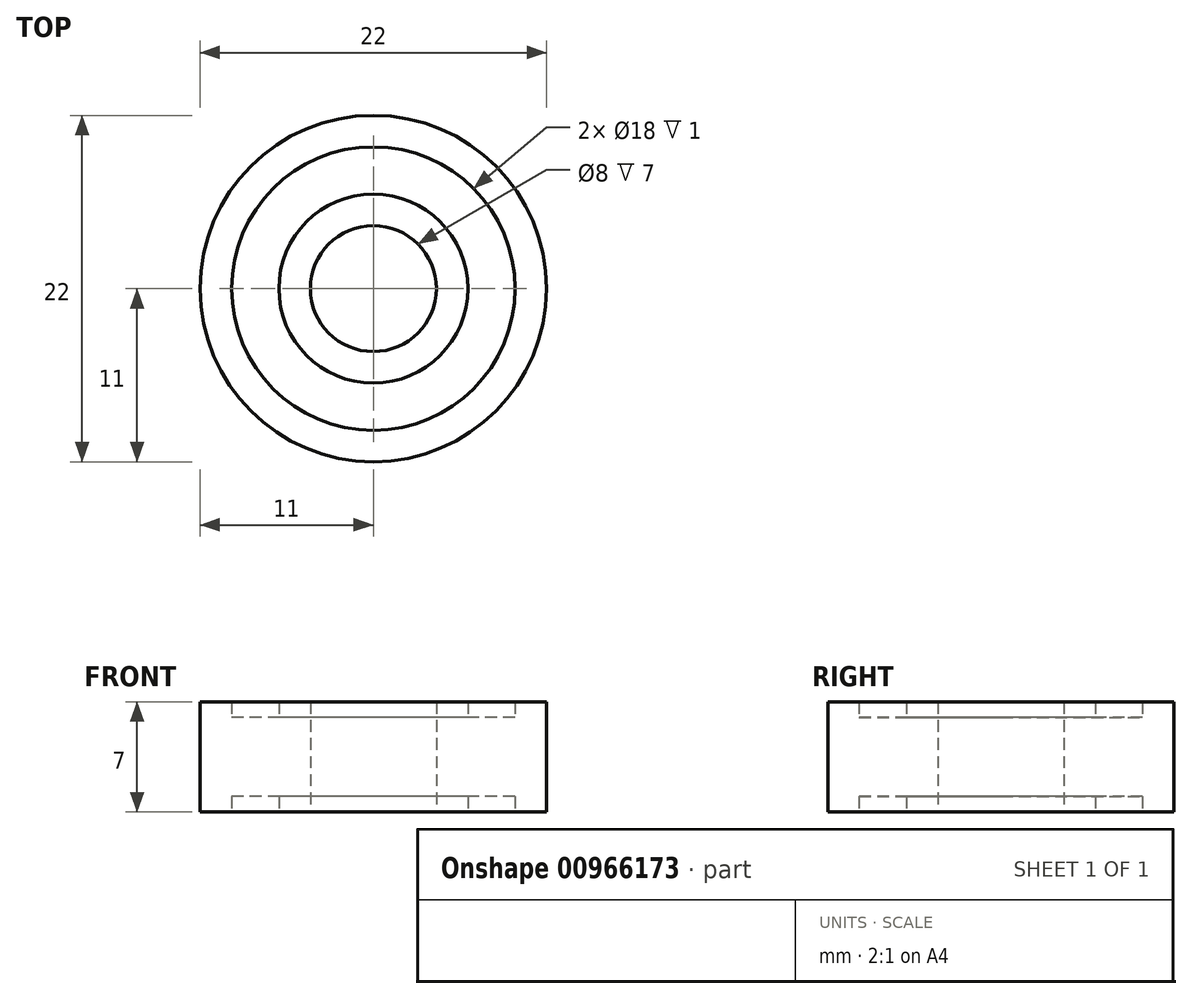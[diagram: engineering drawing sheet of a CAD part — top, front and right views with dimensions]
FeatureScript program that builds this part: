
annotation { "Feature Type Name" : "Feature", "Feature Type Description" : "" }
export const myFeature = defineFeature(function(context is Context, id is Id, definition is map)
    precondition{}
    {
        {
            var Q0;
            Q0=qCreatedBy(makeId("Top.planeOp"),FACE);
            var sketch = newSketch(context, id + "F0", { "sketchPlane" : qUnion([Q0])});
            skCircle(sketch, "E0", {"center": v(0, 0) * mm, "radius": 11 * mm});
            skCircle(sketch, "E1", {"center": v(0, 0) * mm, "radius": 4 * mm});
            skCircle(sketch, "E2", {"center": v(0, 0) * mm, "radius": 9 * mm});
            skCircle(sketch, "E3", {"center": v(0, 0) * mm, "radius": 6 * mm});
            skSolve(sketch);
        }
        {
            var Q0;
            Q0=makeQuery(id+"F0.imprint","IMPRINT",FACE,{"disambiguationData":[TD([[makeQuery(id+"F0.imprint","IMPRINT",EDGE,{"derivedFrom":sQuery(id+"F0.wireOp",EDGE,"E0")}),1.0]])]});
            var Q1;
            Q1=makeQuery(id+"F0.imprint","IMPRINT",FACE,{"disambiguationData":[TD([[makeQuery(id+"F0.imprint","IMPRINT",EDGE,{"derivedFrom":sQuery(id+"F0.wireOp",EDGE,"E1")}),-1.0]])]});
            extrude(context, id + "F1", {"entities" : qUnion([Q0, Q1]), "depth" : 7 * mm, "offsetDistance" : 25 * mm});
        }
        {
            var Q0;
            Q0=makeQuery(id+"F0.imprint","IMPRINT",FACE,{"disambiguationData":[TD([[makeQuery(id+"F0.imprint","IMPRINT",EDGE,{"derivedFrom":sQuery(id+"F0.wireOp",EDGE,"E2")}),1.0]])]});
            extrude(context, id + "F2", {"entities" : qUnion([Q0]), "operationType" : NewBodyOperationType.ADD, "depth" : 6 * mm, "offsetDistance" : 25 * mm, "hasSecondDirection" : true, "secondDirectionOppositeDirection" : false, "secondDirectionDepth" : 1 * mm});
        }
    });
